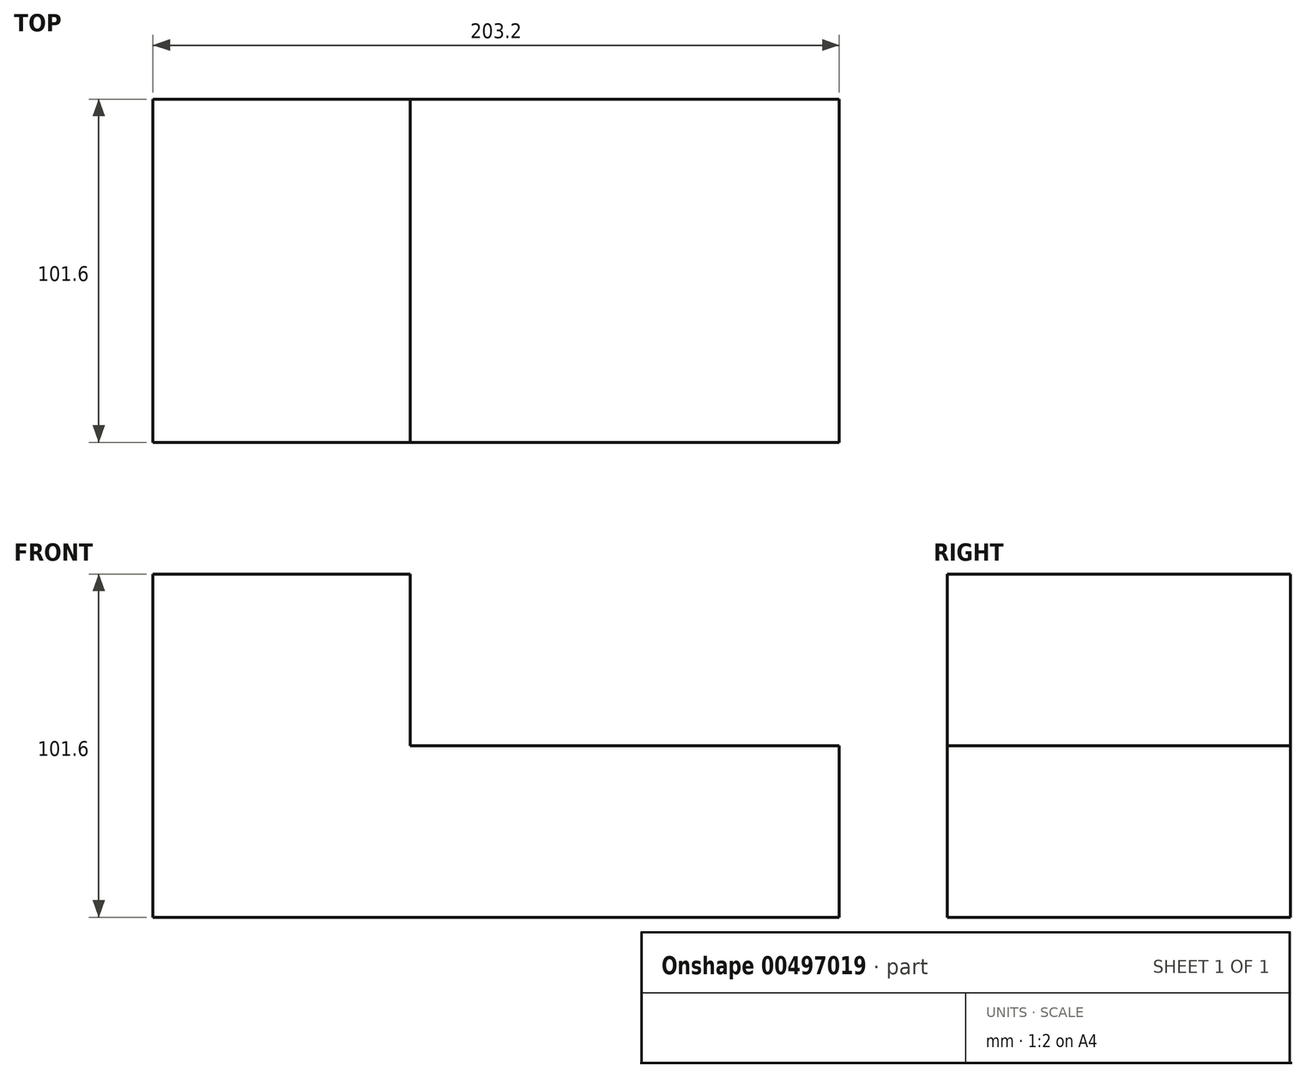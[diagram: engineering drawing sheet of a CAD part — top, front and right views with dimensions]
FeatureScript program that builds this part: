
annotation { "Feature Type Name" : "Feature", "Feature Type Description" : "" }
export const myFeature = defineFeature(function(context is Context, id is Id, definition is map)
    precondition{}
    {
        {
            var Q0;
            Q0=qCreatedBy(makeId("Front.planeOp"),FACE);
            var sketch = newSketch(context, id + "F0", { "sketchPlane" : qUnion([Q0])});
            skLineSegment(sketch, "E0.bottom", {"start": v(0, 0) * mm, "end": v(203.2, 0) * mm});
            skLineSegment(sketch, "E0.top", {"start": v(0, 101.6) * mm, "end": v(76.2, 101.6) * mm});
            skLineSegment(sketch, "E0.left", {"start": v(0, 0) * mm, "end": v(0, 101.6) * mm});
            skLineSegment(sketch, "E0.right", {"start": v(203.2, 0) * mm, "end": v(203.2, 50.8) * mm});
            skLineSegment(sketch, "E1", {"start": v(0, 50.8) * mm, "end": v(203.2, 50.8) * mm});
            skLineSegment(sketch, "E2", {"start": v(0, 50.8) * mm, "end": v(76.2, 50.8) * mm});
            skLineSegment(sketch, "E3", {"start": v(76.2, 50.8) * mm, "end": v(76.2, 101.6) * mm});
            skPoint(sketch, "E4.orphan", {"position": v(203.2, 101.6) * mm});
            skSolve(sketch);
        }
        {
            var Q0;
            Q0 = qSketchRegion(id + "F0", true);
            extrude(context, id + "F1", {"entities" : qUnion([Q0]), "oppositeDirection" : true, "depth" : 101.6 * mm});
        }
    });
